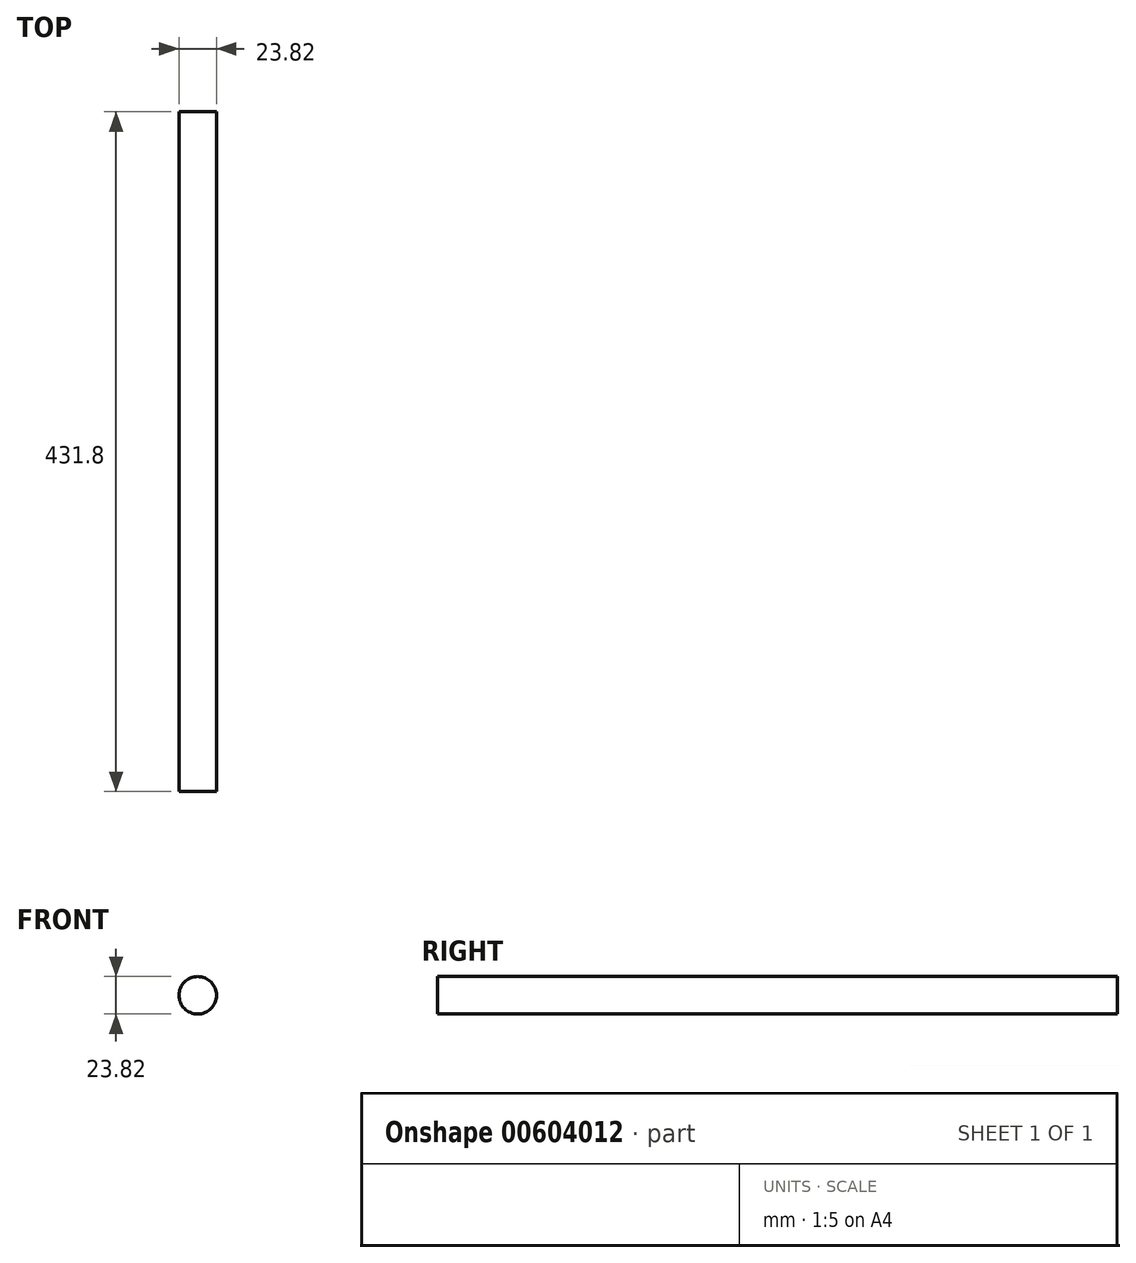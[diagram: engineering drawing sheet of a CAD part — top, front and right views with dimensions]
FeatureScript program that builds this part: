
annotation { "Feature Type Name" : "Feature", "Feature Type Description" : "" }
export const myFeature = defineFeature(function(context is Context, id is Id, definition is map)
    precondition{}
    {
        {
            var Q0;
            Q0=qCreatedBy(makeId("Front.planeOp"),FACE);
            var sketch = newSketch(context, id + "F0", { "sketchPlane" : qUnion([Q0])});
            skCircle(sketch, "E0", {"center": v(0, 0) * mm, "radius": 11.9 * mm});
            skSolve(sketch);
        }
        {
            var Q0;
            Q0 = qSketchRegion(id + "F0", true);
            extrude(context, id + "F1", {"entities" : qUnion([Q0]), "depth" : 431.8 * mm, "offsetDistance" : 25 * mm});
        }
    });
